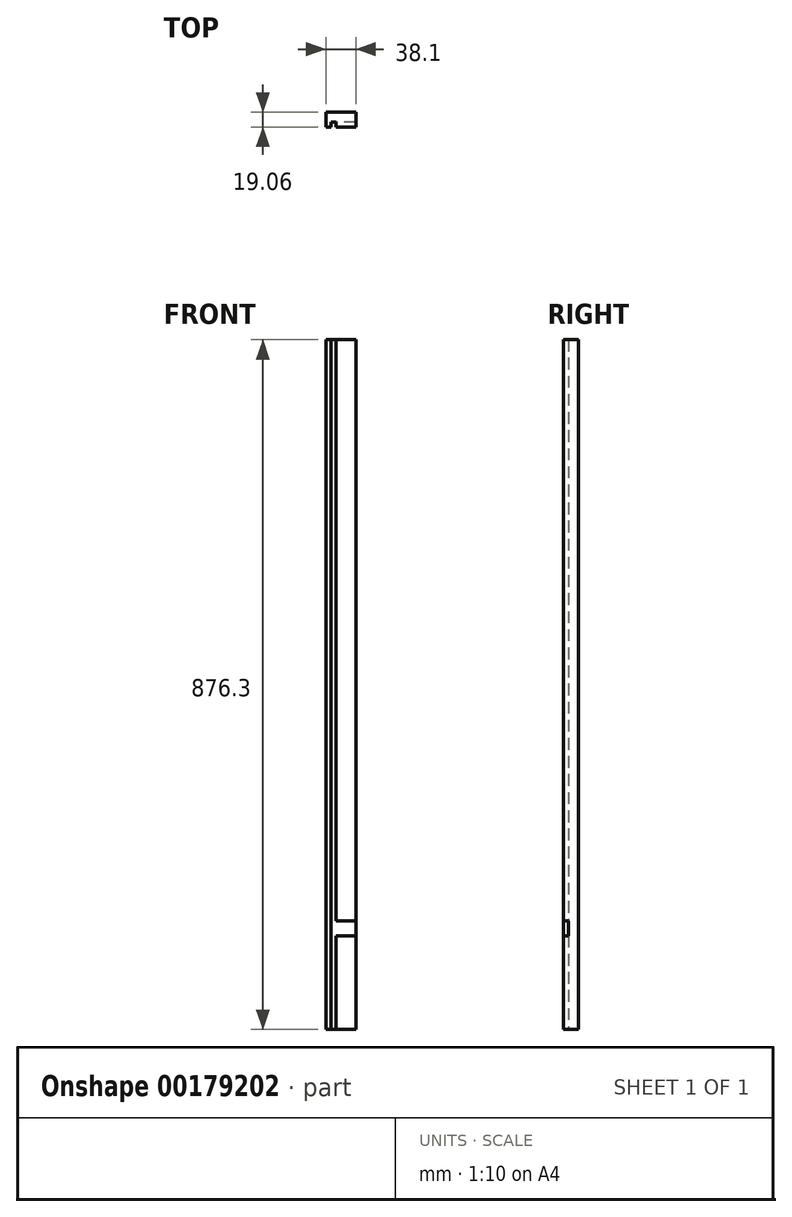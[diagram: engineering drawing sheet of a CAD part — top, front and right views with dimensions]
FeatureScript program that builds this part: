
annotation { "Feature Type Name" : "Feature", "Feature Type Description" : "" }
export const myFeature = defineFeature(function(context is Context, id is Id, definition is map)
    precondition{}
    {
        {
            var Q0;
            Q0=qCreatedBy(makeId("Front.planeOp"),FACE);
            var sketch = newSketch(context, id + "F0", { "sketchPlane" : qUnion([Q0])});
            skLineSegment(sketch, "E0.bottom", {"start": v(-32, 438.15) * mm, "end": v(6.1, 438.15) * mm});
            skLineSegment(sketch, "E0.top", {"start": v(-32, -438.15) * mm, "end": v(6.1, -438.15) * mm});
            skLineSegment(sketch, "E0.left", {"start": v(-32, 438.15) * mm, "end": v(-32, -438.15) * mm});
            skLineSegment(sketch, "E0.right", {"start": v(6.1, 438.15) * mm, "end": v(6.1, -438.15) * mm});
            skLineSegment(sketch, "E1", {"start": v(-32, 0) * mm, "end": v(6.1, 0) * mm});
            skSolve(sketch);
        }
        {
            var Q0;
            {var subQ0=sQuery(id+"F0.wireOp",EDGE,"E0.bottom");Q0=makeQuery(id+"F0.imprint","IMPRINT",FACE,{"disambiguationData":[TD([[makeQuery(id+"F0.imprint","IMPRINT",EDGE,{"derivedFrom":subQ0}),-1.0]])]});}
            var Q1;
            {var subQ0=sQuery(id+"F0.wireOp",EDGE,"E0.top");Q1=makeQuery(id+"F0.imprint","IMPRINT",FACE,{"disambiguationData":[TD([[makeQuery(id+"F0.imprint","IMPRINT",EDGE,{"derivedFrom":subQ0}),1.0]])]});}
            extrude(context, id + "F1", {"entities" : qUnion([Q0, Q1]), "depth" : 19.05 * mm, "symmetric" : true});
        }
        {
            var Q0;
            Q0=makeQuery(id+"F1.opExtrude","CAP_FACE",FACE,{"disambiguationData":[OSD([sQuery(id+"F0.wireOp",EDGE,"E0.bottom"),sQuery(id+"F0.wireOp",EDGE,"E0.top"),sQuery(id+"F0.wireOp",EDGE,"E0.left"),sQuery(id+"F0.wireOp",EDGE,"E0.right")])],"isStart":false});
            var sketch = newSketch(context, id + "F2", { "sketchPlane" : qUnion([Q0])});
            skLineSegment(sketch, "E2.bottom", {"start": v(-25.65, 438.15) * mm, "end": v(-19.3, 438.15) * mm});
            skLineSegment(sketch, "E2.top", {"start": v(-25.65, -438.15) * mm, "end": v(-19.3, -438.15) * mm});
            skLineSegment(sketch, "E2.left", {"start": v(-25.65, 438.15) * mm, "end": v(-25.65, -438.15) * mm});
            skLineSegment(sketch, "E2.right", {"start": v(-19.3, 438.15) * mm, "end": v(-19.3, -438.15) * mm});
            skSolve(sketch);
        }
        {
            var Q0;
            Q0=makeQuery(id+"F2.imprint","IMPRINT",FACE,{"disambiguationData":[TD([[makeQuery(id+"F2.imprint","IMPRINT",EDGE,{"derivedFrom":sQuery(id+"F2.wireOp",EDGE,"E2.bottom")}),-1.0]])]});
            extrude(context, id + "F3", {"entities" : qUnion([Q0]), "operationType" : NewBodyOperationType.REMOVE, "oppositeDirection" : true, "depth" : 6.35 * mm});
        }
        {
            var Q0;
            {var subQ0=sQuery(id+"F0.wireOp",EDGE,"E0.bottom");var subQ1=sQuery(id+"F0.wireOp",EDGE,"E0.top");var subQ2=sQuery(id+"F0.wireOp",EDGE,"E0.right");Q0=makeQuery(id+"F3.boolean.opBoolean","SPLIT",FACE,{"disambiguationData":[TD([makeQuery(id+"F1.opExtrude","SWEPT_FACE",FACE,{"disambiguationData":[OSD([subQ2])]})])],"derivedFrom":makeQuery(id+"F1.opExtrude","CAP_FACE",FACE,{"disambiguationData":[OSD([subQ0,subQ1,sQuery(id+"F0.wireOp",EDGE,"E0.left"),subQ2])],"isStart":false})});}
            var sketch = newSketch(context, id + "F4", { "sketchPlane" : qUnion([Q0])});
            skLineSegment(sketch, "E3.bottom", {"start": v(-19.3, 336.55) * mm, "end": v(6.1, 336.55) * mm});
            skLineSegment(sketch, "E3.top", {"start": v(-19.3, 317.5) * mm, "end": v(6.1, 317.5) * mm});
            skLineSegment(sketch, "E3.left", {"start": v(-19.3, 336.55) * mm, "end": v(-19.3, 317.5) * mm});
            skLineSegment(sketch, "E3.right", {"start": v(6.1, 336.55) * mm, "end": v(6.1, 317.5) * mm});
            skSolve(sketch);
        }
        {
            var Q0;
            {var subQ0=sQuery(id+"F4.wireOp",EDGE,"E3.top");Q0=makeQuery(id+"F4.imprint","IMPRINT",FACE,{"disambiguationData":[TD([[makeQuery(id+"F4.imprint","IMPRINT",EDGE,{"derivedFrom":subQ0}),-1.0]])]});}
            var sketch = newSketch(context, id + "F5", { "sketchPlane" : qUnion([Q0])});
            skLineSegment(sketch, "E4.bottom", {"start": v(6.1, -319.09) * mm, "end": v(-19.3, -319.09) * mm});
            skLineSegment(sketch, "E4.top", {"start": v(6.1, -300.04) * mm, "end": v(-19.3, -300.04) * mm});
            skLineSegment(sketch, "E4.left", {"start": v(6.1, -319.09) * mm, "end": v(6.1, -300.04) * mm});
            skLineSegment(sketch, "E4.right", {"start": v(-19.3, -319.09) * mm, "end": v(-19.3, -300.04) * mm});
            skSolve(sketch);
        }
        {
            var Q0;
            Q0 = qSketchRegion(id + "F5", true);
            extrude(context, id + "F6", {"entities" : qUnion([Q0]), "operationType" : NewBodyOperationType.REMOVE, "oppositeDirection" : true, "depth" : 6.35 * mm});
        }
    });
